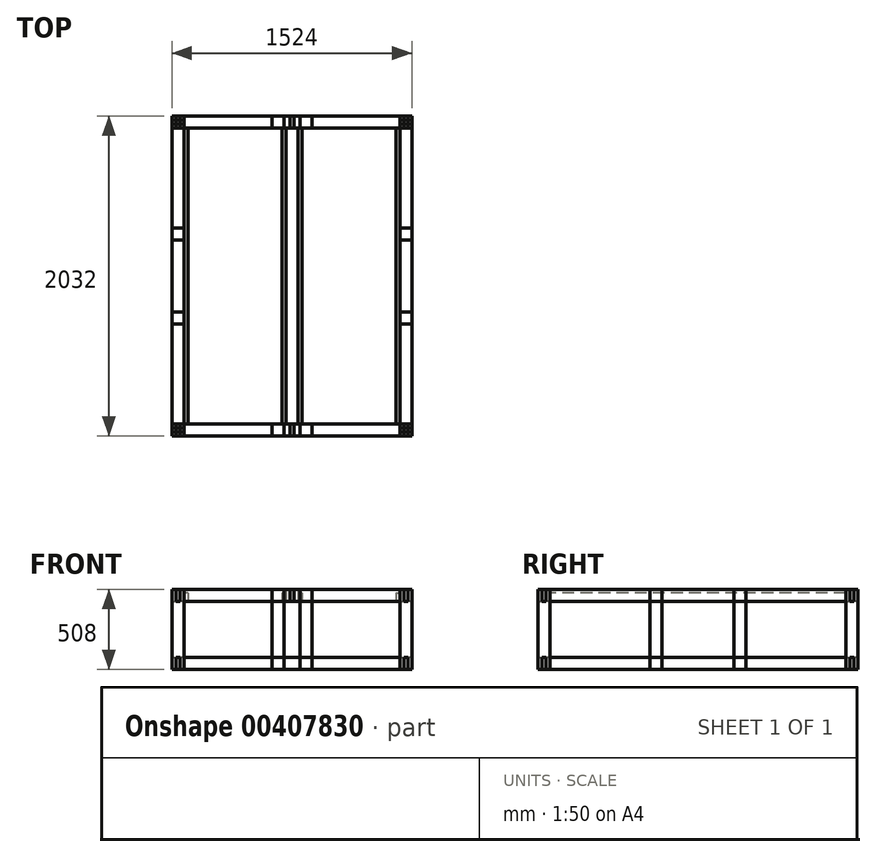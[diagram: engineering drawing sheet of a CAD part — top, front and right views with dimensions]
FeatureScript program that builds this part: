
annotation { "Feature Type Name" : "Feature", "Feature Type Description" : "" }
export const myFeature = defineFeature(function(context is Context, id is Id, definition is map)
    precondition{}
    {
        {
            var Q0;
            Q0=qCreatedBy(makeId("Top.planeOp"),FACE);
            var sketch = newSketch(context, id + "F0", { "sketchPlane" : qUnion([Q0])});
            skLineSegment(sketch, "E0.bottom", {"start": v(-762, 1016) * mm, "end": v(762, 1016) * mm, "construction": true});
            skLineSegment(sketch, "E0.top", {"start": v(-762, -1016) * mm, "end": v(762, -1016) * mm, "construction": true});
            skLineSegment(sketch, "E0.left", {"start": v(-762, 1016) * mm, "end": v(-762, -1016) * mm, "construction": true});
            skLineSegment(sketch, "E0.right", {"start": v(762, 1016) * mm, "end": v(762, -1016) * mm, "construction": true});
            skPoint(sketch, "E0.middle", {"position": v(0, 0) * mm});
            skSolve(sketch);
        }
        {
            var Q0;
            Q0=qCreatedBy(makeId("Top.planeOp"),FACE);
            var sketch = newSketch(context, id + "F1", { "sketchPlane" : qUnion([Q0])});
            skLineSegment(sketch, "E1.0", {"start": v(-685.8, 1016) * mm, "end": v(685.8, 1016) * mm});
            skLineSegment(sketch, "E2.0", {"start": v(-685.8, 939.8) * mm, "end": v(685.8, 939.8) * mm});
            skLineSegment(sketch, "E3", {"start": v(-762, 990.6) * mm, "end": v(-762, 965.2) * mm});
            skLineSegment(sketch, "E4", {"start": v(762, 990.6) * mm, "end": v(762, 965.2) * mm});
            skLineSegment(sketch, "E5", {"start": v(685.8, 939.8) * mm, "end": v(685.8, 965.2) * mm});
            skLineSegment(sketch, "E6", {"start": v(685.8, 965.2) * mm, "end": v(762, 965.2) * mm});
            skLineSegment(sketch, "E7", {"start": v(685.8, 1016) * mm, "end": v(685.8, 990.6) * mm});
            skLineSegment(sketch, "E8", {"start": v(685.8, 990.6) * mm, "end": v(762, 990.6) * mm});
            skPoint(sketch, "E9.orphan", {"position": v(762, 1016) * mm});
            skLineSegment(sketch, "E10", {"start": v(-685.8, 939.8) * mm, "end": v(-685.8, 965.2) * mm});
            skLineSegment(sketch, "E11", {"start": v(-685.8, 965.2) * mm, "end": v(-762, 965.2) * mm});
            skLineSegment(sketch, "E12", {"start": v(-685.8, 1016) * mm, "end": v(-685.8, 990.6) * mm});
            skLineSegment(sketch, "E13", {"start": v(-685.8, 990.6) * mm, "end": v(-762, 990.6) * mm});
            skPoint(sketch, "E14.orphan", {"position": v(-762, 1016) * mm});
            skSolve(sketch);
        }
        {
            var Q0;
            Q0 = qSketchRegion(id + "F1", true);
            extrude(context, id + "F2", {"entities" : qUnion([Q0]), "depth" : 76.2 * mm});
        }
        {
            var Q0;
            Q0=qCreatedBy(makeId("Top.planeOp"),FACE);
            var sketch = newSketch(context, id + "F3", { "sketchPlane" : qUnion([Q0])});
            skLineSegment(sketch, "E15.0", {"start": v(762, 939.8) * mm, "end": v(762, -939.8) * mm});
            skLineSegment(sketch, "E16.0", {"start": v(685.8, 939.8) * mm, "end": v(685.8, -939.8) * mm});
            skLineSegment(sketch, "E17", {"start": v(711.2, 1016) * mm, "end": v(736.6, 1016) * mm});
            skLineSegment(sketch, "E18", {"start": v(711.2, -1016) * mm, "end": v(736.6, -1016) * mm});
            skLineSegment(sketch, "E19", {"start": v(762, 939.8) * mm, "end": v(736.6, 939.8) * mm});
            skLineSegment(sketch, "E20", {"start": v(736.6, 939.8) * mm, "end": v(736.6, 1016) * mm});
            skLineSegment(sketch, "E21", {"start": v(685.8, 939.8) * mm, "end": v(711.2, 939.8) * mm});
            skLineSegment(sketch, "E22", {"start": v(711.2, 939.8) * mm, "end": v(711.2, 1016) * mm});
            skPoint(sketch, "E23.orphan", {"position": v(762, 1016) * mm});
            skLineSegment(sketch, "E24", {"start": v(762, -939.8) * mm, "end": v(736.6, -939.8) * mm});
            skLineSegment(sketch, "E25", {"start": v(736.6, -939.8) * mm, "end": v(736.6, -1016) * mm});
            skLineSegment(sketch, "E26", {"start": v(685.8, -939.8) * mm, "end": v(711.2, -939.8) * mm});
            skLineSegment(sketch, "E27", {"start": v(711.2, -939.8) * mm, "end": v(711.2, -1016) * mm});
            skPoint(sketch, "E28.orphan", {"position": v(762, -1016) * mm});
            skSolve(sketch);
        }
        {
            var Q0;
            Q0 = qSketchRegion(id + "F3", true);
            extrude(context, id + "F4", {"entities" : qUnion([Q0]), "depth" : 76.2 * mm});
        }
        {
            var Q0;
            Q0=qCreatedBy(makeId("Top.planeOp"),FACE);
            var sketch = newSketch(context, id + "F5", { "sketchPlane" : qUnion([Q0])});
            skLineSegment(sketch, "E29.0", {"start": v(-38.1, 1016) * mm, "end": v(38.1, 1016) * mm});
            skLineSegment(sketch, "E30.0", {"start": v(-12.7, 1016) * mm, "end": v(12.7, 1016) * mm});
            skLineSegment(sketch, "E31.top", {"start": v(-12.7, -1016) * mm, "end": v(12.7, -1016) * mm});
            skLineSegment(sketch, "E31.left", {"start": v(-38.1, 939.8) * mm, "end": v(-38.1, -939.8) * mm});
            skLineSegment(sketch, "E31.right", {"start": v(38.1, 939.8) * mm, "end": v(38.1, -939.8) * mm});
            skPoint(sketch, "E31.middle", {"position": v(0, 0) * mm});
            skLineSegment(sketch, "E32.0", {"start": v(-38.1, 939.8) * mm, "end": v(38.1, 939.8) * mm});
            skLineSegment(sketch, "E33", {"start": v(12.7, 939.8) * mm, "end": v(12.7, 1016) * mm});
            skLineSegment(sketch, "E34", {"start": v(-12.7, 1016) * mm, "end": v(-12.7, 939.8) * mm});
            skPoint(sketch, "E35.orphan", {"position": v(-685.8, 939.8) * mm});
            skPoint(sketch, "E36.orphan", {"position": v(38.1, 1016) * mm});
            skPoint(sketch, "E37.orphan", {"position": v(685.8, 939.8) * mm});
            skPoint(sketch, "E38.orphan", {"position": v(-38.1, 1016) * mm});
            skLineSegment(sketch, "E39.trimOffspring", {"start": v(38.1, 1016) * mm, "end": v(685.8, 1016) * mm});
            skPoint(sketch, "E40.orphan", {"position": v(-685.8, 1016) * mm});
            skLineSegment(sketch, "E41", {"start": v(12.7, -1016) * mm, "end": v(12.7, -939.8) * mm});
            skLineSegment(sketch, "E42", {"start": v(12.7, -939.8) * mm, "end": v(38.1, -939.8) * mm});
            skLineSegment(sketch, "E43", {"start": v(-38.1, -939.8) * mm, "end": v(-12.7, -939.8) * mm});
            skLineSegment(sketch, "E44", {"start": v(-12.7, -939.8) * mm, "end": v(-12.7, -1016) * mm});
            skPoint(sketch, "E45.orphan", {"position": v(-38.1, -1016) * mm});
            skPoint(sketch, "E46.orphan", {"position": v(38.1, -1016) * mm});
            skSolve(sketch);
        }
        {
            var Q0;
            Q0 = qSketchRegion(id + "F5", true);
            extrude(context, id + "F6", {"entities" : qUnion([Q0]), "depth" : 76.2 * mm});
        }
        {
            var Q0;
            Q0=qCreatedBy(makeId("Top.planeOp"),FACE);
            var sketch = newSketch(context, id + "F7", { "sketchPlane" : qUnion([Q0])});
            skLineSegment(sketch, "E47.0", {"start": v(685.8, 939.8) * mm, "end": v(685.8, -939.8) * mm});
            skLineSegment(sketch, "E48.0", {"start": v(38.1, 939.8) * mm, "end": v(38.1, -939.8) * mm});
            skLineSegment(sketch, "E49.0", {"start": v(63.5, 939.8) * mm, "end": v(63.5, -939.8) * mm});
            skLineSegment(sketch, "E50.0", {"start": v(660.4, 939.8) * mm, "end": v(660.4, -939.8) * mm});
            skLineSegment(sketch, "E51", {"start": v(63.5, 939.8) * mm, "end": v(38.1, 939.8) * mm});
            skLineSegment(sketch, "E52", {"start": v(660.4, 939.8) * mm, "end": v(685.8, 939.8) * mm});
            skLineSegment(sketch, "E53", {"start": v(63.5, -939.8) * mm, "end": v(38.1, -939.8) * mm});
            skLineSegment(sketch, "E54", {"start": v(660.4, -939.8) * mm, "end": v(685.8, -939.8) * mm});
            skSolve(sketch);
        }
        {
            var Q0;
            Q0 = qSketchRegion(id + "F7", true);
            extrude(context, id + "F8", {"entities" : qUnion([Q0]), "depth" : 53.97 * mm});
        }
        {
            var Q0;
            Q0=makeQuery(id+"F2.opExtrude","CAP_FACE",FACE,{"disambiguationData":[OSD([sQuery(id+"F1.wireOp",EDGE,"E1.0"),sQuery(id+"F1.wireOp",EDGE,"E2.0"),sQuery(id+"F1.wireOp",EDGE,"E3"),sQuery(id+"F1.wireOp",EDGE,"E4"),sQuery(id+"F1.wireOp",EDGE,"E5"),sQuery(id+"F1.wireOp",EDGE,"E6"),sQuery(id+"F1.wireOp",EDGE,"E7"),sQuery(id+"F1.wireOp",EDGE,"E8"),sQuery(id+"F1.wireOp",EDGE,"E10"),sQuery(id+"F1.wireOp",EDGE,"E11"),sQuery(id+"F1.wireOp",EDGE,"E12"),sQuery(id+"F1.wireOp",EDGE,"E13")])],"isStart":false});
            var sketch = newSketch(context, id + "F9", { "sketchPlane" : qUnion([Q0])});
            skLineSegment(sketch, "E55.0", {"start": v(685.8, 1016) * mm, "end": v(685.8, 939.8) * mm});
            skLineSegment(sketch, "E56.0", {"start": v(762, 939.8) * mm, "end": v(685.8, 939.8) * mm});
            skLineSegment(sketch, "E57.0", {"start": v(685.8, 1016) * mm, "end": v(762, 1016) * mm});
            skLineSegment(sketch, "E58.0", {"start": v(762, 1016) * mm, "end": v(762, 939.8) * mm});
            skPoint(sketch, "E59.orphan", {"position": v(762, -1016) * mm});
            skPoint(sketch, "E60.orphan", {"position": v(-762, 1016) * mm});
            skSolve(sketch);
        }
        {
            var Q0;
            Q0 = qSketchRegion(id + "F9", true);
            extrude(context, id + "F10", {"entities" : qUnion([Q0]), "oppositeDirection" : true, "depth" : 508 * mm});
        }
        {
            var Q0;
            Q0=qCreatedBy(makeId("Top.planeOp"),FACE);
            cPlane(context, id + "F11", {"entities" : qUnion([Q0]), "cplaneType" : CPlaneType.OFFSET, "offset" : 177.8 * mm, "oppositeDirection" : true, "width" : 152.4 * mm, "height" : 152.4 * mm});
        }
        {
            var Q0;
            Q0=makeQuery(id+"F2.opExtrude","SWEPT_FACE",FACE,{"disambiguationData":[OSD([sQuery(id+"F1.wireOp",EDGE,"E1.0")])]});
            var sketch = newSketch(context, id + "F12", { "sketchPlane" : qUnion([Q0])});
            skLineSegment(sketch, "E61.bottom", {"start": v(-127, 76.2) * mm, "end": v(-50.8, 76.2) * mm});
            skLineSegment(sketch, "E61.top", {"start": v(-127, -431.8) * mm, "end": v(-50.8, -431.8) * mm});
            skLineSegment(sketch, "E61.left", {"start": v(-127, 76.2) * mm, "end": v(-127, -431.8) * mm});
            skLineSegment(sketch, "E61.right", {"start": v(-50.8, 76.2) * mm, "end": v(-50.8, -431.8) * mm});
            skSolve(sketch);
        }
        {
            var Q0;
            Q0 = qSketchRegion(id + "F12", true);
            extrude(context, id + "F13", {"entities" : qUnion([Q0]), "oppositeDirection" : true, "depth" : 76.2 * mm});
        }
        {
            var Q0;
            Q0=makeQuery(id+"F4.opExtrude","SWEPT_FACE",FACE,{"disambiguationData":[OSD([sQuery(id+"F3.wireOp",EDGE,"E15.0")])]});
            var sketch = newSketch(context, id + "F14", { "sketchPlane" : qUnion([Q0])});
            skLineSegment(sketch, "E62.bottom", {"start": v(228.6, 76.2) * mm, "end": v(304.8, 76.2) * mm});
            skLineSegment(sketch, "E62.top", {"start": v(228.6, -431.8) * mm, "end": v(304.8, -431.8) * mm});
            skLineSegment(sketch, "E62.left", {"start": v(228.6, 76.2) * mm, "end": v(228.6, -431.8) * mm});
            skLineSegment(sketch, "E62.right", {"start": v(304.8, 76.2) * mm, "end": v(304.8, -431.8) * mm});
            skSolve(sketch);
        }
        {
            var Q0;
            Q0 = qSketchRegion(id + "F14", true);
            extrude(context, id + "F15", {"entities" : qUnion([Q0]), "oppositeDirection" : true, "depth" : 76.2 * mm});
        }
        {
            var Q0;
            Q0=makeQuery(id+"F2.opExtrude","SWEPT_BODY",BODY,{"disambiguationData":[OSD([sQuery(id+"F1.wireOp",EDGE,"E1.0"),sQuery(id+"F1.wireOp",EDGE,"E2.0"),sQuery(id+"F1.wireOp",EDGE,"E3"),sQuery(id+"F1.wireOp",EDGE,"E4"),sQuery(id+"F1.wireOp",EDGE,"E5"),sQuery(id+"F1.wireOp",EDGE,"E6"),sQuery(id+"F1.wireOp",EDGE,"E7"),sQuery(id+"F1.wireOp",EDGE,"E8"),sQuery(id+"F1.wireOp",EDGE,"E10"),sQuery(id+"F1.wireOp",EDGE,"E11"),sQuery(id+"F1.wireOp",EDGE,"E12"),sQuery(id+"F1.wireOp",EDGE,"E13")])]});
            var Q1;
            Q1=makeQuery(id+"F13.opExtrude","SWEPT_BODY",BODY,{"disambiguationData":[OSD([sQuery(id+"F12.wireOp",EDGE,"E61.bottom"),sQuery(id+"F12.wireOp",EDGE,"E61.top"),sQuery(id+"F12.wireOp",EDGE,"E61.left"),sQuery(id+"F12.wireOp",EDGE,"E61.right")])]});
            var Q2;
            Q2=makeQuery(id+"F10.opExtrude","SWEPT_BODY",BODY,{"disambiguationData":[OSD([sQuery(id+"F9.wireOp",EDGE,"E55.0"),sQuery(id+"F9.wireOp",EDGE,"E56.0"),sQuery(id+"F9.wireOp",EDGE,"E57.0"),sQuery(id+"F9.wireOp",EDGE,"E58.0")])]});
            var Q3;
            Q3=makeQuery(id+"F15.opExtrude","SWEPT_BODY",BODY,{"disambiguationData":[OSD([sQuery(id+"F14.wireOp",EDGE,"E62.bottom"),sQuery(id+"F14.wireOp",EDGE,"E62.top"),sQuery(id+"F14.wireOp",EDGE,"E62.left"),sQuery(id+"F14.wireOp",EDGE,"E62.right")])]});
            var Q4;
            Q4=qCreatedBy(makeId("Front.planeOp"),FACE);
            mirror(context, id + "F16", {"entities" : qUnion([Q0, Q1, Q2, Q3]), "mirrorPlane" : qUnion([Q4])});
        }
        {
            var Q0;
            Q0=makeQuery(id+"F16.opPattern","COPY",BODY,{"derivedFrom":makeQuery(id+"F10.opExtrude","SWEPT_BODY",BODY,{"disambiguationData":[OSD([sQuery(id+"F9.wireOp",EDGE,"E55.0"),sQuery(id+"F9.wireOp",EDGE,"E56.0"),sQuery(id+"F9.wireOp",EDGE,"E57.0"),sQuery(id+"F9.wireOp",EDGE,"E58.0")])]}),"instanceName":"1"});
            var Q1;
            Q1=makeQuery(id+"F16.opPattern","COPY",BODY,{"derivedFrom":makeQuery(id+"F13.opExtrude","SWEPT_BODY",BODY,{"disambiguationData":[OSD([sQuery(id+"F12.wireOp",EDGE,"E61.bottom"),sQuery(id+"F12.wireOp",EDGE,"E61.top"),sQuery(id+"F12.wireOp",EDGE,"E61.left"),sQuery(id+"F12.wireOp",EDGE,"E61.right")])]}),"instanceName":"1"});
            var Q2;
            Q2=makeQuery(id+"F16.opPattern","COPY",BODY,{"derivedFrom":makeQuery(id+"F15.opExtrude","SWEPT_BODY",BODY,{"disambiguationData":[OSD([sQuery(id+"F14.wireOp",EDGE,"E62.bottom"),sQuery(id+"F14.wireOp",EDGE,"E62.top"),sQuery(id+"F14.wireOp",EDGE,"E62.left"),sQuery(id+"F14.wireOp",EDGE,"E62.right")])]}),"instanceName":"1"});
            var Q3;
            Q3=makeQuery(id+"F15.opExtrude","SWEPT_BODY",BODY,{"disambiguationData":[OSD([sQuery(id+"F14.wireOp",EDGE,"E62.bottom"),sQuery(id+"F14.wireOp",EDGE,"E62.top"),sQuery(id+"F14.wireOp",EDGE,"E62.left"),sQuery(id+"F14.wireOp",EDGE,"E62.right")])]});
            var Q4;
            Q4=makeQuery(id+"F10.opExtrude","SWEPT_BODY",BODY,{"disambiguationData":[OSD([sQuery(id+"F9.wireOp",EDGE,"E55.0"),sQuery(id+"F9.wireOp",EDGE,"E56.0"),sQuery(id+"F9.wireOp",EDGE,"E57.0"),sQuery(id+"F9.wireOp",EDGE,"E58.0")])]});
            var Q5;
            Q5=makeQuery(id+"F13.opExtrude","SWEPT_BODY",BODY,{"disambiguationData":[OSD([sQuery(id+"F12.wireOp",EDGE,"E61.bottom"),sQuery(id+"F12.wireOp",EDGE,"E61.top"),sQuery(id+"F12.wireOp",EDGE,"E61.left"),sQuery(id+"F12.wireOp",EDGE,"E61.right")])]});
            var Q6;
            Q6=makeQuery(id+"F8.opExtrude","SWEPT_BODY",BODY,{"disambiguationData":[OSD([sQuery(id+"F7.wireOp",EDGE,"E48.0"),sQuery(id+"F7.wireOp",EDGE,"E49.0"),sQuery(id+"F7.wireOp",EDGE,"E51"),sQuery(id+"F7.wireOp",EDGE,"E53")])]});
            var Q7;
            Q7=makeQuery(id+"F8.opExtrude","SWEPT_BODY",BODY,{"disambiguationData":[OSD([sQuery(id+"F7.wireOp",EDGE,"E47.0"),sQuery(id+"F7.wireOp",EDGE,"E50.0"),sQuery(id+"F7.wireOp",EDGE,"E52"),sQuery(id+"F7.wireOp",EDGE,"E54")])]});
            var Q8;
            Q8=makeQuery(id+"F4.opExtrude","SWEPT_BODY",BODY,{"disambiguationData":[OSD([sQuery(id+"F3.wireOp",EDGE,"E15.0"),sQuery(id+"F3.wireOp",EDGE,"E16.0"),sQuery(id+"F3.wireOp",EDGE,"E17"),sQuery(id+"F3.wireOp",EDGE,"E18"),sQuery(id+"F3.wireOp",EDGE,"E19"),sQuery(id+"F3.wireOp",EDGE,"E20"),sQuery(id+"F3.wireOp",EDGE,"E21"),sQuery(id+"F3.wireOp",EDGE,"E22"),sQuery(id+"F3.wireOp",EDGE,"E24"),sQuery(id+"F3.wireOp",EDGE,"E25"),sQuery(id+"F3.wireOp",EDGE,"E26"),sQuery(id+"F3.wireOp",EDGE,"E27")])]});
            var Q9;
            Q9=qCreatedBy(makeId("Right.planeOp"),FACE);
            mirror(context, id + "F17", {"entities" : qUnion([Q0, Q1, Q2, Q3, Q4, Q5, Q6, Q7, Q8]), "mirrorPlane" : qUnion([Q9])});
        }
        {
            var Q0;
            Q0=makeQuery(id+"F16.opPattern","COPY",BODY,{"derivedFrom":makeQuery(id+"F2.opExtrude","SWEPT_BODY",BODY,{"disambiguationData":[OSD([sQuery(id+"F1.wireOp",EDGE,"E1.0"),sQuery(id+"F1.wireOp",EDGE,"E2.0"),sQuery(id+"F1.wireOp",EDGE,"E3"),sQuery(id+"F1.wireOp",EDGE,"E4"),sQuery(id+"F1.wireOp",EDGE,"E5"),sQuery(id+"F1.wireOp",EDGE,"E6"),sQuery(id+"F1.wireOp",EDGE,"E7"),sQuery(id+"F1.wireOp",EDGE,"E8"),sQuery(id+"F1.wireOp",EDGE,"E10"),sQuery(id+"F1.wireOp",EDGE,"E11"),sQuery(id+"F1.wireOp",EDGE,"E12"),sQuery(id+"F1.wireOp",EDGE,"E13")])]}),"instanceName":"1"});
            var Q1;
            Q1=makeQuery(id+"F4.opExtrude","SWEPT_BODY",BODY,{"disambiguationData":[OSD([sQuery(id+"F3.wireOp",EDGE,"E15.0"),sQuery(id+"F3.wireOp",EDGE,"E16.0"),sQuery(id+"F3.wireOp",EDGE,"E17"),sQuery(id+"F3.wireOp",EDGE,"E18"),sQuery(id+"F3.wireOp",EDGE,"E19"),sQuery(id+"F3.wireOp",EDGE,"E20"),sQuery(id+"F3.wireOp",EDGE,"E21"),sQuery(id+"F3.wireOp",EDGE,"E22"),sQuery(id+"F3.wireOp",EDGE,"E24"),sQuery(id+"F3.wireOp",EDGE,"E25"),sQuery(id+"F3.wireOp",EDGE,"E26"),sQuery(id+"F3.wireOp",EDGE,"E27")])]});
            var Q2;
            Q2=makeQuery(id+"F2.opExtrude","SWEPT_BODY",BODY,{"disambiguationData":[OSD([sQuery(id+"F1.wireOp",EDGE,"E1.0"),sQuery(id+"F1.wireOp",EDGE,"E2.0"),sQuery(id+"F1.wireOp",EDGE,"E3"),sQuery(id+"F1.wireOp",EDGE,"E4"),sQuery(id+"F1.wireOp",EDGE,"E5"),sQuery(id+"F1.wireOp",EDGE,"E6"),sQuery(id+"F1.wireOp",EDGE,"E7"),sQuery(id+"F1.wireOp",EDGE,"E8"),sQuery(id+"F1.wireOp",EDGE,"E10"),sQuery(id+"F1.wireOp",EDGE,"E11"),sQuery(id+"F1.wireOp",EDGE,"E12"),sQuery(id+"F1.wireOp",EDGE,"E13")])]});
            var Q3;
            Q3=makeQuery(id+"F17.opPattern","COPY",BODY,{"derivedFrom":makeQuery(id+"F4.opExtrude","SWEPT_BODY",BODY,{"disambiguationData":[OSD([sQuery(id+"F3.wireOp",EDGE,"E15.0"),sQuery(id+"F3.wireOp",EDGE,"E16.0"),sQuery(id+"F3.wireOp",EDGE,"E17"),sQuery(id+"F3.wireOp",EDGE,"E18"),sQuery(id+"F3.wireOp",EDGE,"E19"),sQuery(id+"F3.wireOp",EDGE,"E20"),sQuery(id+"F3.wireOp",EDGE,"E21"),sQuery(id+"F3.wireOp",EDGE,"E22"),sQuery(id+"F3.wireOp",EDGE,"E24"),sQuery(id+"F3.wireOp",EDGE,"E25"),sQuery(id+"F3.wireOp",EDGE,"E26"),sQuery(id+"F3.wireOp",EDGE,"E27")])]}),"instanceName":"1"});
            var Q4;
            Q4=qCreatedBy(id+"F11.planeOp",FACE);
            mirror(context, id + "F18", {"entities" : qUnion([Q0, Q1, Q2, Q3]), "mirrorPlane" : qUnion([Q4])});
        }
    });
